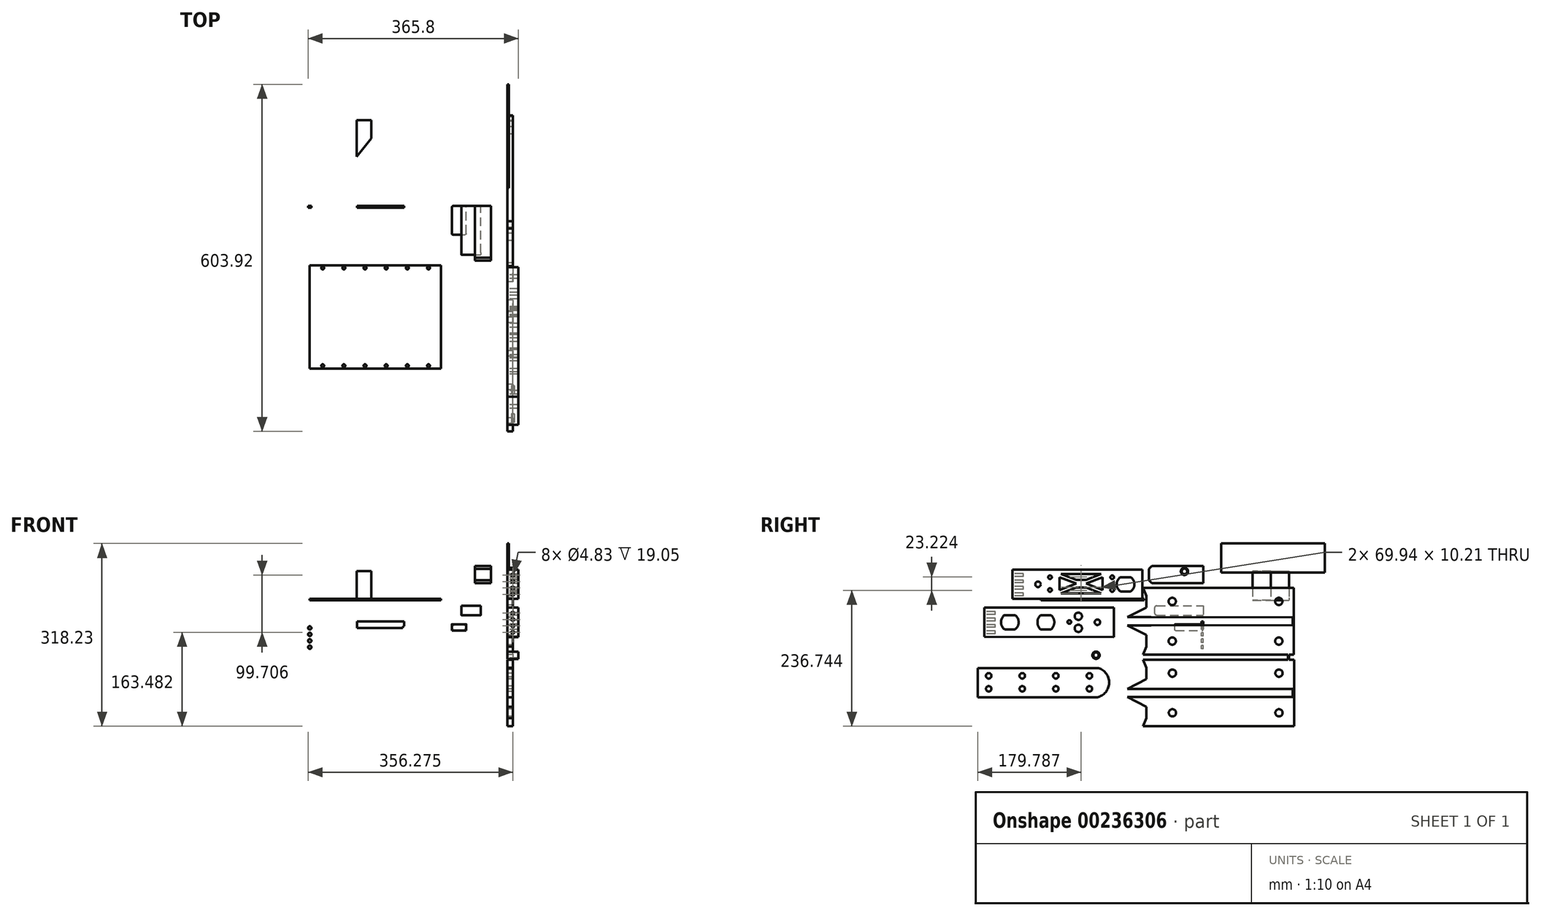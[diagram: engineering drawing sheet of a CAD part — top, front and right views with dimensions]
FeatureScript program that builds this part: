
annotation { "Feature Type Name" : "Feature", "Feature Type Description" : "" }
export const myFeature = defineFeature(function(context is Context, id is Id, definition is map)
    precondition{}
    {
        {
            var Q0;
            Q0=qCreatedBy(makeId("Right.planeOp"),FACE);
            var sketch = newSketch(context, id + "F0", { "sketchPlane" : qUnion([Q0])});
            skPoint(sketch, "E0.1.0.8", {"position": v(-472.48, 27.53) * mm});
            skCircle(sketch, "E1", {"center": v(-287.76, 28) * mm, "radius": 4.76 * mm});
            skLineSegment(sketch, "E2", {"start": v(-233.08, 52.93) * mm, "end": v(-233.08, 40.2) * mm});
            skPoint(sketch, "E2.endSnap0", {"position": v(-233.08, 52.93) * mm});
            skPoint(sketch, "E3.MirrorP", {"position": v(6.32, 27.53) * mm});
            skLineSegment(sketch, "E4", {"start": v(-106.44, 2.48) * mm, "end": v(-332.21, 2.71) * mm});
            skLineSegment(sketch, "E5", {"start": v(-106.44, 53.64) * mm, "end": v(-332.21, 53.6) * mm});
            skCircle(sketch, "E6", {"center": v(-135.36, 28) * mm, "radius": 6.35 * mm});
            skLineSegment(sketch, "E7", {"start": v(-106.44, 53.64) * mm, "end": v(-106.44, 2.48) * mm});
            skPoint(sketch, "E8", {"position": v(-106.44, 28.06) * mm});
            skLineSegment(sketch, "E9", {"start": v(-332.21, 53.6) * mm, "end": v(-332.21, 2.71) * mm});
            skLineSegment(sketch, "E10.bottom", {"start": v(-144.38, 40.44) * mm, "end": v(-126.35, 40.44) * mm});
            skLineSegment(sketch, "E10.top", {"start": v(-144.38, 15.55) * mm, "end": v(-126.35, 15.55) * mm});
            skLineSegment(sketch, "E10.left", {"start": v(-144.38, 40.44) * mm, "end": v(-144.38, 15.55) * mm});
            skLineSegment(sketch, "E10.right", {"start": v(-126.35, 40.44) * mm, "end": v(-126.35, 15.55) * mm});
            skLineSegment(sketch, "E11", {"start": v(-135.36, 15.55) * mm, "end": v(-135.36, 24.56) * mm});
            skArc(sketch, "E12", {"start": v(-126.35, 15.55) * mm, "mid": v(-119.96, 28) * mm, "end": v(-126.35, 40.44) * mm});
            skArc(sketch, "E13.MirrorCS", {"start": v(-144.38, 15.55) * mm, "mid": v(-150.77, 28) * mm, "end": v(-144.38, 40.44) * mm});
            skSolve(sketch);
        }
        {
            var Q0;
            Q0=makeQuery(id+"F0.imprint","IMPRINT",FACE,{"disambiguationData":[TD([[makeQuery(id+"F0.imprint","IMPRINT",EDGE,{"derivedFrom":sQuery(id+"F0.wireOp",EDGE,"48NEkoHX-YDjR-4glP-9xDk-O7jPTVT27snB.bottom")}),-1.0]])]});
            var Q1;
            Q1=makeQuery(id+"F0.imprint","IMPRINT",FACE,{"disambiguationData":[TD([[makeQuery(id+"F0.imprint","IMPRINT",EDGE,{"derivedFrom":sQuery(id+"F0.wireOp",EDGE,"6096469f-17e3-4775-aaf3-049bcc5bdd68.0.1.0")}),1.0]])]});
            var Q2;
            Q2=makeQuery(id+"F0.imprint","IMPRINT",FACE,{"disambiguationData":[TD([[makeQuery(id+"F0.imprint","IMPRINT",EDGE,{"derivedFrom":sQuery(id+"F0.wireOp",EDGE,"6096469f-17e3-4775-aaf3-049bcc5bdd68.0.2.0")}),1.0]])]});
            var Q3;
            Q3=makeQuery(id+"F0.imprint","IMPRINT",FACE,{"disambiguationData":[TD([[makeQuery(id+"F0.imprint","IMPRINT",EDGE,{"derivedFrom":sQuery(id+"F0.wireOp",EDGE,"4wjqRqQA-ueKa-S8QN-2kGj-S2SypDfkeyo9.bottom")}),1.0]])]});
            var Q4;
            Q4=makeQuery(id+"F0.imprint","IMPRINT",FACE,{"disambiguationData":[TD([[makeQuery(id+"F0.imprint","IMPRINT",EDGE,{"derivedFrom":sQuery(id+"F0.wireOp",EDGE,"E0.1.0.1")}),-1.0]])]});
            var Q5;
            Q5=makeQuery(id+"F0.imprint","IMPRINT",FACE,{"disambiguationData":[TD([[makeQuery(id+"F0.imprint","IMPRINT",EDGE,{"derivedFrom":sQuery(id+"F0.wireOp",EDGE,"E1")}),-1.0]])]});
            extrude(context, id + "F1", {"entities" : qUnion([Q0, Q1, Q2, Q3, Q4, Q5]), "depth" : 19.05 * mm});
        }
        {
            var Q0;
            Q0=qCreatedBy(makeId("Right.planeOp"),FACE);
            var sketch = newSketch(context, id + "F2", { "sketchPlane" : qUnion([Q0])});
            skCircle(sketch, "E14", {"center": v(-32.9, 50.41) * mm, "radius": 6.35 * mm});
            skCircle(sketch, "E15", {"center": v(-32.9, 50.41) * mm, "radius": 4.76 * mm});
            skSolve(sketch);
        }
        {
            var Q0;
            Q0 = qSketchRegion(id + "F2", true);
            extrude(context, id + "F3", {"entities" : qUnion([Q0]), "depth" : 9.52 * mm});
        }
        {
            var Q0;
            Q0=qCreatedBy(makeId("Right.planeOp"),FACE);
            var sketch = newSketch(context, id + "F4", { "sketchPlane" : qUnion([Q0])});
            skCircle(sketch, "E16", {"center": v(-54.1, -1.8) * mm, "radius": 6.35 * mm});
            skLineSegment(sketch, "E17", {"start": v(33.95, 20.92) * mm, "end": v(33.95, 8.2) * mm});
            skPoint(sketch, "E17.endSnap0", {"position": v(33.95, 20.92) * mm});
            skLineSegment(sketch, "E18", {"start": v(157.46, -29.52) * mm, "end": v(-90.95, -29.25) * mm});
            skLineSegment(sketch, "E19", {"start": v(157.46, 21.64) * mm, "end": v(-90.94, 21.6) * mm});
            skCircle(sketch, "E20", {"center": v(131.33, -1.8) * mm, "radius": 6.35 * mm});
            skLineSegment(sketch, "E21", {"start": v(157.46, 21.64) * mm, "end": v(157.46, -29.52) * mm});
            skLineSegment(sketch, "E22", {"start": v(-90.94, 21.6) * mm, "end": v(-104.93, 21.6) * mm});
            skLineSegment(sketch, "E23", {"start": v(-104.93, 21.6) * mm, "end": v(-99.24, 7.67) * mm});
            skLineSegment(sketch, "E24", {"start": v(-99.24, -12.44) * mm, "end": v(-132.22, -29.25) * mm});
            skLineSegment(sketch, "E25", {"start": v(-132.22, -29.25) * mm, "end": v(-90.95, -29.25) * mm});
            skLineSegment(sketch, "E26", {"start": v(-99.24, 7.67) * mm, "end": v(-99.24, -12.44) * mm});
            skPoint(sketch, "E27", {"position": v(157.46, -3.94) * mm});
            skLineSegment(sketch, "E28", {"start": v(157.46, -29.52) * mm, "end": v(157.46, -43.14) * mm});
            skLineSegment(sketch, "E29", {"start": v(157.46, -36.33) * mm, "end": v(164.9, -36.33) * mm});
            skLineSegment(sketch, "E30.MirrorCS", {"start": v(33.95, -93.58) * mm, "end": v(33.95, -80.86) * mm});
            skLineSegment(sketch, "E31.MirrorCS", {"start": v(-90.94, -94.26) * mm, "end": v(-104.93, -94.26) * mm});
            skLineSegment(sketch, "E32.MirrorCS", {"start": v(-99.24, -60.22) * mm, "end": v(-132.22, -43.41) * mm});
            skLineSegment(sketch, "E33.MirrorCS", {"start": v(157.46, -94.3) * mm, "end": v(157.46, -43.14) * mm});
            skLineSegment(sketch, "E34.MirrorCS", {"start": v(-104.93, -94.26) * mm, "end": v(-99.24, -80.33) * mm});
            skPoint(sketch, "E35.MirrorP", {"position": v(33.95, -93.58) * mm});
            skPoint(sketch, "E36.MirrorP", {"position": v(157.46, -68.72) * mm});
            skCircle(sketch, "E37.MirrorC", {"center": v(-54.1, -70.86) * mm, "radius": 6.35 * mm});
            skCircle(sketch, "E38.MirrorC", {"center": v(131.33, -70.86) * mm, "radius": 6.35 * mm});
            skLineSegment(sketch, "E39.MirrorCS", {"start": v(157.46, -94.3) * mm, "end": v(-90.94, -94.26) * mm});
            skLineSegment(sketch, "E40.MirrorCS", {"start": v(157.46, -43.14) * mm, "end": v(-90.95, -43.41) * mm});
            skLineSegment(sketch, "E41.MirrorCS", {"start": v(-99.24, -80.33) * mm, "end": v(-99.24, -60.22) * mm});
            skLineSegment(sketch, "E42.MirrorCS", {"start": v(-132.22, -43.41) * mm, "end": v(-90.95, -43.41) * mm});
            skLineSegment(sketch, "E43", {"start": v(155.23, -29.52) * mm, "end": v(155.22, -43.14) * mm});
            skLineSegment(sketch, "E44", {"start": v(155.23, -34.67) * mm, "end": v(157.46, -34.67) * mm});
            skCircle(sketch, "E45", {"center": v(-53.77, -126.66) * mm, "radius": 6.35 * mm});
            skLineSegment(sketch, "E46", {"start": v(34.26, -103.93) * mm, "end": v(34.26, -116.65) * mm});
            skPoint(sketch, "E46.endSnap0", {"position": v(34.26, -103.93) * mm});
            skLineSegment(sketch, "E47", {"start": v(157.78, -154.38) * mm, "end": v(-90.63, -154.1) * mm});
            skLineSegment(sketch, "E48", {"start": v(157.78, -103.22) * mm, "end": v(-90.63, -103.25) * mm});
            skCircle(sketch, "E49", {"center": v(131.65, -126.66) * mm, "radius": 6.35 * mm});
            skLineSegment(sketch, "E50", {"start": v(157.78, -103.22) * mm, "end": v(157.78, -154.38) * mm});
            skLineSegment(sketch, "E51", {"start": v(-90.63, -103.25) * mm, "end": v(-104.6, -103.25) * mm});
            skLineSegment(sketch, "E52", {"start": v(-104.6, -103.25) * mm, "end": v(-98.92, -117.18) * mm});
            skLineSegment(sketch, "E53", {"start": v(-98.92, -137.3) * mm, "end": v(-131.9, -154.1) * mm});
            skLineSegment(sketch, "E54", {"start": v(-131.9, -154.1) * mm, "end": v(-90.63, -154.1) * mm});
            skLineSegment(sketch, "E55", {"start": v(-98.92, -117.18) * mm, "end": v(-98.92, -137.3) * mm});
            skPoint(sketch, "E56", {"position": v(157.78, -128.8) * mm});
            skLineSegment(sketch, "E57", {"start": v(157.78, -154.38) * mm, "end": v(157.78, -168) * mm});
            skLineSegment(sketch, "E58", {"start": v(157.78, -161.19) * mm, "end": v(165.2, -161.19) * mm});
            skLineSegment(sketch, "E59.MirrorCS", {"start": v(34.26, -218.44) * mm, "end": v(34.26, -205.72) * mm});
            skLineSegment(sketch, "E60.MirrorCS", {"start": v(-90.63, -219.12) * mm, "end": v(-104.6, -219.12) * mm});
            skLineSegment(sketch, "E61.MirrorCS", {"start": v(-98.92, -185.08) * mm, "end": v(-131.9, -168.27) * mm});
            skLineSegment(sketch, "E62.MirrorCS", {"start": v(157.78, -219.15) * mm, "end": v(157.78, -168) * mm});
            skLineSegment(sketch, "E63.MirrorCS", {"start": v(-104.6, -219.12) * mm, "end": v(-98.92, -205.19) * mm});
            skPoint(sketch, "E64.MirrorP", {"position": v(34.26, -218.44) * mm});
            skPoint(sketch, "E65.MirrorP", {"position": v(157.78, -193.57) * mm});
            skCircle(sketch, "E66.MirrorC", {"center": v(-53.77, -195.71) * mm, "radius": 6.35 * mm});
            skCircle(sketch, "E67.MirrorC", {"center": v(131.65, -195.71) * mm, "radius": 6.35 * mm});
            skLineSegment(sketch, "E68.MirrorCS", {"start": v(157.78, -219.15) * mm, "end": v(-90.63, -219.12) * mm});
            skLineSegment(sketch, "E69.MirrorCS", {"start": v(157.78, -168) * mm, "end": v(-90.63, -168.27) * mm});
            skLineSegment(sketch, "E70.MirrorCS", {"start": v(-98.92, -205.19) * mm, "end": v(-98.92, -185.08) * mm});
            skLineSegment(sketch, "E71.MirrorCS", {"start": v(-131.9, -168.27) * mm, "end": v(-90.63, -168.27) * mm});
            skLineSegment(sketch, "E72", {"start": v(155.55, -154.37) * mm, "end": v(155.54, -168) * mm});
            skLineSegment(sketch, "E73", {"start": v(155.54, -159.52) * mm, "end": v(157.78, -159.53) * mm});
            skLineSegment(sketch, "E74", {"start": v(148.89, -94.3) * mm, "end": v(148.88, -103.22) * mm});
            skLineSegment(sketch, "E75", {"start": v(147.48, -94.3) * mm, "end": v(147.48, -103.22) * mm});
            skSolve(sketch);
        }
        {
            var Q0;
            Q0 = qSketchRegion(id + "F4", true);
            extrude(context, id + "F5", {"entities" : qUnion([Q0]), "depth" : 9.52 * mm});
        }
        {
            var Q0;
            Q0=qCreatedBy(makeId("Right.planeOp"),FACE);
            var sketch = newSketch(context, id + "F6", { "sketchPlane" : qUnion([Q0])});
            skLineSegment(sketch, "E76", {"start": v(-275.22, -14.07) * mm, "end": v(-275.22, -26.8) * mm});
            skPoint(sketch, "E76.endSnap0", {"position": v(-275.22, -14.07) * mm});
            skLineSegment(sketch, "E77", {"start": v(-155.4, -63.65) * mm, "end": v(-381.17, -63.42) * mm});
            skLineSegment(sketch, "E78", {"start": v(-155.4, -12.5) * mm, "end": v(-381.17, -12.57) * mm});
            skCircle(sketch, "E79", {"center": v(-184.32, -38.07) * mm, "radius": 4.76 * mm});
            skLineSegment(sketch, "E80", {"start": v(-155.4, -12.5) * mm, "end": v(-155.4, -63.65) * mm});
            skPoint(sketch, "E81", {"position": v(-155.4, -38.07) * mm});
            skLineSegment(sketch, "E82", {"start": v(-381.17, -12.57) * mm, "end": v(-381.17, -63.42) * mm});
            skLineSegment(sketch, "E83.bottom", {"start": v(-345.74, -25.63) * mm, "end": v(-327.7, -25.63) * mm});
            skLineSegment(sketch, "E83.top", {"start": v(-345.74, -50.52) * mm, "end": v(-327.7, -50.52) * mm});
            skLineSegment(sketch, "E83.left", {"start": v(-345.74, -25.63) * mm, "end": v(-345.74, -50.52) * mm});
            skLineSegment(sketch, "E83.right", {"start": v(-327.7, -25.63) * mm, "end": v(-327.7, -50.52) * mm});
            skPoint(sketch, "E83.middle", {"position": v(-336.72, -38.08) * mm});
            skLineSegment(sketch, "E84", {"start": v(-336.72, -50.52) * mm, "end": v(-336.72, -39.25) * mm});
            skArc(sketch, "E85", {"start": v(-327.7, -50.52) * mm, "mid": v(-321.32, -38.08) * mm, "end": v(-327.7, -25.63) * mm});
            skArc(sketch, "E86.MirrorCS", {"start": v(-345.74, -50.52) * mm, "mid": v(-352.12, -38.08) * mm, "end": v(-345.74, -25.63) * mm});
            skSolve(sketch);
        }
        {
            var Q0;
            Q0=makeQuery(id+"F6.imprint","IMPRINT",FACE,{"disambiguationData":[TD([[makeQuery(id+"F6.imprint","IMPRINT",EDGE,{"derivedFrom":sQuery(id+"F6.wireOp",EDGE,"E77")}),-1.0]])]});
            extrude(context, id + "F7", {"entities" : qUnion([Q0]), "depth" : 19.05 * mm});
        }
        {
            var Q0;
            Q0=qCreatedBy(makeId("Front.planeOp"),FACE);
            var sketch = newSketch(context, id + "F8", { "sketchPlane" : qUnion([Q0])});
            skLineSegment(sketch, "E87.bottom", {"start": v(-56.23, 29.85) * mm, "end": v(-28.23, 29.85) * mm});
            skLineSegment(sketch, "E87.top", {"start": v(-56.23, 59.85) * mm, "end": v(-28.23, 59.85) * mm});
            skLineSegment(sketch, "E87.left", {"start": v(-56.23, 29.85) * mm, "end": v(-56.23, 59.85) * mm});
            skLineSegment(sketch, "E87.right", {"start": v(-28.23, 29.85) * mm, "end": v(-28.23, 59.85) * mm});
            skSolve(sketch);
        }
        {
            var Q0;
            Q0 = qSketchRegion(id + "F8", true);
            extrude(context, id + "F9", {"entities" : qUnion([Q0]), "depth" : 95 * mm});
        }
        {
            var Q0;
            Q0=makeQuery(id+"F9.opExtrude","CAP_EDGE",EDGE,{"disambiguationData":[OSD([sQuery(id+"F8.wireOp",EDGE,"E87.top")])],"isStart":false});
            var Q1;
            Q1=makeQuery(id+"F9.opExtrude","CAP_EDGE",EDGE,{"disambiguationData":[OSD([sQuery(id+"F8.wireOp",EDGE,"E87.bottom")])],"isStart":false});
            chamfer(context, id + "F10", {"entities" : qUnion([Q0, Q1]), "width" : 5.08 * mm, "tangentPropagation" : true});
        }
        {
            var Q0;
            Q0=qCreatedBy(makeId("Right.planeOp"),FACE);
            var sketch = newSketch(context, id + "F11", { "sketchPlane" : qUnion([Q0])});
            skCircle(sketch, "E88", {"center": v(-186.77, -95.44) * mm, "radius": 4.76 * mm});
            skCircle(sketch, "E89", {"center": v(-186.77, -95.44) * mm, "radius": 6.35 * mm});
            skSolve(sketch);
        }
        {
            var Q0;
            Q0 = qSketchRegion(id + "F11", true);
            extrude(context, id + "F12", {"entities" : qUnion([Q0]), "depth" : 19.05 * mm});
        }
        {
            var Q0;
            Q0=qCreatedBy(makeId("Front.planeOp"),FACE);
            var sketch = newSketch(context, id + "F13", { "sketchPlane" : qUnion([Q0])});
            skLineSegment(sketch, "E90.bottom", {"start": v(-96.57, -36.56) * mm, "end": v(-426.77, -36.56) * mm});
            skLineSegment(sketch, "E90.top", {"start": v(-96.57, -100.06) * mm, "end": v(-426.77, -100.06) * mm});
            skLineSegment(sketch, "E90.left", {"start": v(-96.57, -36.56) * mm, "end": v(-96.57, -100.06) * mm});
            skLineSegment(sketch, "E90.right", {"start": v(-426.77, -36.56) * mm, "end": v(-426.77, -100.06) * mm});
            skPoint(sketch, "E90.middle", {"position": v(-261.67, -68.31) * mm});
            skSolve(sketch);
        }
        {
            var Q0;
            Q0 = qSketchRegion(id + "F13", true);
            extrude(context, id + "F14", {"entities" : qUnion([Q0]), "depth" : 3.17 * mm});
        }
        {
            var Q0;
            Q0=makeQuery(id+"F7.opExtrude","SWEPT_FACE",FACE,{"disambiguationData":[OSD([sQuery(id+"F6.wireOp",EDGE,"E82")])]});
            var sketch = newSketch(context, id + "F15", { "sketchPlane" : qUnion([Q0])});
            skCircle(sketch, "E91", {"center": v(9.53, -22.14) * mm, "radius": 2.41 * mm});
            skPoint(sketch, "E91.centerSnap0", {"position": v(9.53, -12.57) * mm});
            skPoint(sketch, "E92.centerSnap0", {"position": v(9.53, -63.42) * mm});
            skCircle(sketch, "E93.0.1.0", {"center": v(9.53, -33.32) * mm, "radius": 2.41 * mm});
            skCircle(sketch, "E93.0.2.0", {"center": v(9.53, -44.5) * mm, "radius": 2.41 * mm});
            skCircle(sketch, "E93.0.3.0", {"center": v(9.53, -55.67) * mm, "radius": 2.41 * mm});
            skLineSegment(sketch, "E93.direction1", {"start": v(9.53, -22.14) * mm, "end": v(34.93, -22.14) * mm, "construction": true});
            skLineSegment(sketch, "E93.direction2", {"start": v(9.53, -22.14) * mm, "end": v(9.53, -33.32) * mm, "construction": true});
            skSolve(sketch);
        }
        {
            var Q0;
            Q0 = qSketchRegion(id + "F15", true);
            extrude(context, id + "F16", {"entities" : qUnion([Q0]), "operationType" : NewBodyOperationType.REMOVE, "oppositeDirection" : true, "depth" : 19.05 * mm});
        }
        {
            var Q0;
            Q0=makeQuery(id+"F1.opExtrude","SWEPT_FACE",FACE,{"disambiguationData":[OSD([sQuery(id+"F0.wireOp",EDGE,"E9")])]});
            var sketch = newSketch(context, id + "F17", { "sketchPlane" : qUnion([Q0])});
            skCircle(sketch, "E94", {"center": v(9.53, 44.04) * mm, "radius": 2.41 * mm});
            skPoint(sketch, "E94.centerSnap0", {"position": v(9.53, 53.6) * mm});
            skLineSegment(sketch, "E95", {"start": v(9.53, 44.04) * mm, "end": v(9.53, 53.6) * mm});
            skCircle(sketch, "E96.0.1.0", {"center": v(9.53, 32.86) * mm, "radius": 2.41 * mm});
            skCircle(sketch, "E96.0.2.0", {"center": v(9.53, 21.69) * mm, "radius": 2.41 * mm});
            skCircle(sketch, "E96.0.3.0", {"center": v(9.53, 10.51) * mm, "radius": 2.41 * mm});
            skLineSegment(sketch, "E96.direction1", {"start": v(9.53, 44.04) * mm, "end": v(34.93, 44.04) * mm, "construction": true});
            skLineSegment(sketch, "E96.direction2", {"start": v(9.53, 44.04) * mm, "end": v(9.53, 32.86) * mm, "construction": true});
            skSolve(sketch);
        }
        {
            var Q0;
            Q0 = qSketchRegion(id + "F17", true);
            extrude(context, id + "F18", {"entities" : qUnion([Q0]), "operationType" : NewBodyOperationType.REMOVE, "oppositeDirection" : true, "depth" : 19.05 * mm});
        }
        {
            var Q0;
            Q0=makeQuery(id+"F14.opExtrude","CAP_FACE",FACE,{"disambiguationData":[OSD([sQuery(id+"F13.wireOp",EDGE,"E90.bottom"),sQuery(id+"F13.wireOp",EDGE,"E90.top"),sQuery(id+"F13.wireOp",EDGE,"E90.left"),sQuery(id+"F13.wireOp",EDGE,"E90.right")])],"isStart":false});
            var sketch = newSketch(context, id + "F19", { "sketchPlane" : qUnion([Q0])});
            skLineSegment(sketch, "E97", {"start": v(-261.67, -36.56) * mm, "end": v(-261.67, -48) * mm});
            skLineSegment(sketch, "E98", {"start": v(-261.67, -48) * mm, "end": v(-179.52, -48) * mm});
            skLineSegment(sketch, "E99", {"start": v(-179.52, -48) * mm, "end": v(-179.52, -36.56) * mm});
            skCircle(sketch, "E100", {"center": v(-179.52, -48) * mm, "radius": 2.92 * mm});
            skCircle(sketch, "E101.0.1.0", {"center": v(-179.52, -59.17) * mm, "radius": 2.92 * mm});
            skCircle(sketch, "E101.0.2.0", {"center": v(-179.52, -70.34) * mm, "radius": 2.92 * mm});
            skCircle(sketch, "E101.0.3.0", {"center": v(-179.52, -81.52) * mm, "radius": 2.92 * mm});
            skLineSegment(sketch, "E101.direction1", {"start": v(-179.52, -48) * mm, "end": v(-171.82, -48) * mm, "construction": true});
            skLineSegment(sketch, "E101.direction2", {"start": v(-179.52, -48) * mm, "end": v(-179.52, -59.17) * mm, "construction": true});
            skCircle(sketch, "E102.MirrorC", {"center": v(-343.83, -81.52) * mm, "radius": 2.92 * mm});
            skCircle(sketch, "E103.MirrorC", {"center": v(-343.83, -48) * mm, "radius": 2.92 * mm});
            skCircle(sketch, "E104.MirrorC", {"center": v(-343.83, -70.34) * mm, "radius": 2.92 * mm});
            skLineSegment(sketch, "E105.MirrorCS", {"start": v(-343.83, -48) * mm, "end": v(-343.83, -59.17) * mm, "construction": true});
            skCircle(sketch, "E106.MirrorC", {"center": v(-343.83, -59.17) * mm, "radius": 2.92 * mm});
            skSolve(sketch);
        }
        {
            var Q0;
            Q0=makeQuery(id+"F19.imprint","IMPRINT",FACE,{"disambiguationData":[TD([[makeQuery(id+"F19.imprint","IMPRINT",EDGE,{"derivedFrom":sQuery(id+"F19.wireOp",EDGE,"E103.MirrorC")}),-1.0]])]});
            var Q1;
            Q1=makeQuery(id+"F19.imprint","IMPRINT",FACE,{"disambiguationData":[TD([[makeQuery(id+"F19.imprint","IMPRINT",EDGE,{"derivedFrom":sQuery(id+"F19.wireOp",EDGE,"E106.MirrorC")}),-1.0]])]});
            var Q2;
            Q2=makeQuery(id+"F19.imprint","IMPRINT",FACE,{"disambiguationData":[TD([[makeQuery(id+"F19.imprint","IMPRINT",EDGE,{"derivedFrom":sQuery(id+"F19.wireOp",EDGE,"E104.MirrorC")}),-1.0]])]});
            var Q3;
            Q3=makeQuery(id+"F19.imprint","IMPRINT",FACE,{"disambiguationData":[TD([[makeQuery(id+"F19.imprint","IMPRINT",EDGE,{"derivedFrom":sQuery(id+"F19.wireOp",EDGE,"E102.MirrorC")}),-1.0]])]});
            var Q4;
            Q4=makeQuery(id+"F19.imprint","IMPRINT",FACE,{"disambiguationData":[TD([[makeQuery(id+"F19.imprint","IMPRINT",EDGE,{"derivedFrom":sQuery(id+"F19.wireOp",EDGE,"E101.0.2.0")}),1.0]])]});
            var Q5;
            Q5=makeQuery(id+"F19.imprint","IMPRINT",FACE,{"disambiguationData":[TD([[makeQuery(id+"F19.imprint","IMPRINT",EDGE,{"derivedFrom":sQuery(id+"F19.wireOp",EDGE,"E101.0.1.0")}),1.0]])]});
            var Q6;
            {var subQ0=sQuery(id+"F19.wireOp",EDGE,"E99");var subQ1=sQuery(id+"F19.wireOp",EDGE,"E98");var subQ2=makeQuery(id+"F19.imprint","INTERSECT",VERTEX,{"derivedFrom":[subQ1,subQ0]});Q6=makeQuery(id+"F19.imprint","IMPRINT",FACE,{"disambiguationData":[TD([[makeQuery(id+"F19.imprint","IMPRINT",EDGE,{"disambiguationData":[TD([[subQ2,1.0]])],"derivedFrom":subQ1}),-1.0]])]});}
            var Q7;
            Q7=makeQuery(id+"F19.imprint","IMPRINT",FACE,{"disambiguationData":[TD([[makeQuery(id+"F19.imprint","IMPRINT",EDGE,{"derivedFrom":sQuery(id+"F19.wireOp",EDGE,"E101.0.3.0")}),1.0]])]});
            var Q8;
            {var subQ0=sQuery(id+"F19.wireOp",EDGE,"E99");var subQ1=sQuery(id+"F19.wireOp",EDGE,"E98");var subQ2=makeQuery(id+"F19.imprint","INTERSECT",VERTEX,{"derivedFrom":[subQ1,subQ0]});Q8=makeQuery(id+"F19.imprint","IMPRINT",FACE,{"disambiguationData":[TD([[makeQuery(id+"F19.imprint","IMPRINT",EDGE,{"disambiguationData":[TD([[subQ2,1.0]])],"derivedFrom":subQ1}),1.0]])]});}
            var Q9;
            Q9=makeQuery(id+"F14.opExtrude","CAP_FACE",FACE,{"disambiguationData":[OSD([sQuery(id+"F13.wireOp",EDGE,"E90.bottom"),sQuery(id+"F13.wireOp",EDGE,"E90.top"),sQuery(id+"F13.wireOp",EDGE,"E90.left"),sQuery(id+"F13.wireOp",EDGE,"E90.right")])],"isStart":true});
            extrude(context, id + "F20", {"entities" : qUnion([Q0, Q1, Q2, Q3, Q4, Q5, Q6, Q7, Q8]), "operationType" : NewBodyOperationType.REMOVE, "endBound" : BoundingType.UP_TO_SURFACE, "oppositeDirection" : true, "endBoundEntityFace" : qUnion([Q9]), "depth" : 25.4 * mm});
        }
        {
            var Q0;
            Q0=qCreatedBy(makeId("Top.planeOp"),FACE);
            var sketch = newSketch(context, id + "F21", { "sketchPlane" : qUnion([Q0])});
            skLineSegment(sketch, "E107.bottom", {"start": v(-115.3, -103.27) * mm, "end": v(-343.9, -103.27) * mm});
            skLineSegment(sketch, "E107.top", {"start": v(-115.3, -282.94) * mm, "end": v(-343.9, -282.94) * mm});
            skLineSegment(sketch, "E107.left", {"start": v(-115.3, -103.27) * mm, "end": v(-115.3, -282.94) * mm});
            skLineSegment(sketch, "E107.right", {"start": v(-343.9, -103.27) * mm, "end": v(-343.9, -282.94) * mm});
            skSolve(sketch);
        }
        {
            var Q0;
            Q0 = qSketchRegion(id + "F21", true);
            extrude(context, id + "F22", {"entities" : qUnion([Q0]), "depth" : 2.54 * mm});
        }
        {
            var Q0;
            Q0=qCreatedBy(makeId("Front.planeOp"),FACE);
            var sketch = newSketch(context, id + "F23", { "sketchPlane" : qUnion([Q0])});
            skLineSegment(sketch, "E108.bottom", {"start": v(-80, -9.56) * mm, "end": v(-46, -9.56) * mm});
            skLineSegment(sketch, "E108.top", {"start": v(-80, -25.56) * mm, "end": v(-46, -25.56) * mm});
            skLineSegment(sketch, "E108.left", {"start": v(-80, -9.56) * mm, "end": v(-80, -25.56) * mm});
            skLineSegment(sketch, "E108.right", {"start": v(-46, -9.56) * mm, "end": v(-46, -25.56) * mm});
            skSolve(sketch);
        }
        {
            var Q0;
            Q0 = qSketchRegion(id + "F23", true);
            extrude(context, id + "F24", {"entities" : qUnion([Q0]), "depth" : 85 * mm});
        }
        {
            var Q0;
            Q0=makeQuery(id+"F24.opExtrude","CAP_EDGE",EDGE,{"disambiguationData":[OSD([sQuery(id+"F23.wireOp",EDGE,"E108.top")])],"isStart":false});
            var Q1;
            Q1=makeQuery(id+"F24.opExtrude","CAP_EDGE",EDGE,{"disambiguationData":[OSD([sQuery(id+"F23.wireOp",EDGE,"E108.bottom")])],"isStart":false});
            fillet(context, id + "F25", {"entities" : qUnion([Q0, Q1]), "radius" : 3.8 * mm, "tangentPropagation" : true, "allowEdgeOverflow" : false});
        }
        {
            var Q0;
            Q0=qCreatedBy(makeId("Front.planeOp"),FACE);
            var sketch = newSketch(context, id + "F26", { "sketchPlane" : qUnion([Q0])});
            skLineSegment(sketch, "E109.bottom", {"start": v(-96.6, -41.43) * mm, "end": v(-71.6, -41.43) * mm});
            skLineSegment(sketch, "E109.top", {"start": v(-96.6, -52.43) * mm, "end": v(-71.6, -52.43) * mm});
            skLineSegment(sketch, "E109.left", {"start": v(-96.6, -41.43) * mm, "end": v(-96.6, -52.43) * mm});
            skLineSegment(sketch, "E109.right", {"start": v(-71.6, -41.43) * mm, "end": v(-71.6, -52.43) * mm});
            skSolve(sketch);
        }
        {
            var Q0;
            Q0 = qSketchRegion(id + "F26", true);
            extrude(context, id + "F27", {"entities" : qUnion([Q0]), "depth" : 50 * mm});
        }
        {
            var Q0;
            Q0=makeQuery(id+"F27.opExtrude","CAP_EDGE",EDGE,{"disambiguationData":[OSD([sQuery(id+"F26.wireOp",EDGE,"E109.bottom")])],"isStart":false});
            var Q1;
            Q1=makeQuery(id+"F27.opExtrude","CAP_EDGE",EDGE,{"disambiguationData":[OSD([sQuery(id+"F26.wireOp",EDGE,"E109.left")])],"isStart":false});
            var Q2;
            Q2=makeQuery(id+"F27.opExtrude","CAP_EDGE",EDGE,{"disambiguationData":[OSD([sQuery(id+"F26.wireOp",EDGE,"E109.top")])],"isStart":false});
            var Q3;
            Q3=makeQuery(id+"F27.opExtrude","CAP_EDGE",EDGE,{"disambiguationData":[OSD([sQuery(id+"F26.wireOp",EDGE,"E109.right")])],"isStart":false});
            fillet(context, id + "F28", {"entities" : qUnion([Q0, Q1, Q2, Q3]), "radius" : 1.9 * mm, "tangentPropagation" : true, "allowEdgeOverflow" : false});
        }
        {
            var Q0;
            Q0=makeQuery(id+"F27.opExtrude","CAP_EDGE",EDGE,{"disambiguationData":[OSD([sQuery(id+"F26.wireOp",EDGE,"E109.right")])],"isStart":true});
            var Q1;
            Q1=makeQuery(id+"F27.opExtrude","CAP_EDGE",EDGE,{"disambiguationData":[OSD([sQuery(id+"F26.wireOp",EDGE,"E109.bottom")])],"isStart":true});
            var Q2;
            Q2=makeQuery(id+"F27.opExtrude","CAP_EDGE",EDGE,{"disambiguationData":[OSD([sQuery(id+"F26.wireOp",EDGE,"E109.left")])],"isStart":true});
            var Q3;
            Q3=makeQuery(id+"F27.opExtrude","CAP_EDGE",EDGE,{"disambiguationData":[OSD([sQuery(id+"F26.wireOp",EDGE,"E109.top")])],"isStart":true});
            fillet(context, id + "F29", {"entities" : qUnion([Q0, Q1, Q2, Q3]), "radius" : 2.54 * mm, "tangentPropagation" : true, "allowEdgeOverflow" : false});
        }
        {
            var Q0;
            Q0=makeQuery(id+"F7.opExtrude","CAP_FACE",FACE,{"disambiguationData":[OSD([sQuery(id+"F6.wireOp",EDGE,"E77"),sQuery(id+"F6.wireOp",EDGE,"E78"),sQuery(id+"F6.wireOp",EDGE,"E79"),sQuery(id+"F6.wireOp",EDGE,"E80"),sQuery(id+"F6.wireOp",EDGE,"E82"),sQuery(id+"F6.wireOp",EDGE,"E83.bottom"),sQuery(id+"F6.wireOp",EDGE,"E83.top"),sQuery(id+"F6.wireOp",EDGE,"E85"),sQuery(id+"F6.wireOp",EDGE,"E86.MirrorCS")])],"isStart":true});
            var sketch = newSketch(context, id + "F30", { "sketchPlane" : qUnion([Q0])});
            skPoint(sketch, "E110.startSnap0", {"position": v(155.4, -38.07) * mm});
            skLineSegment(sketch, "E111.bottom", {"start": v(283.04, -50.52) * mm, "end": v(264.96, -50.52) * mm});
            skLineSegment(sketch, "E111.top", {"start": v(283.04, -25.63) * mm, "end": v(264.96, -25.63) * mm});
            skLineSegment(sketch, "E111.left", {"start": v(283.04, -50.52) * mm, "end": v(283.04, -25.63) * mm});
            skLineSegment(sketch, "E111.right", {"start": v(264.96, -50.52) * mm, "end": v(264.96, -25.63) * mm});
            skArc(sketch, "E112", {"start": v(264.96, -25.63) * mm, "mid": v(259.33, -38.08) * mm, "end": v(264.96, -50.52) * mm});
            skLineSegment(sketch, "E113", {"start": v(274, -50.52) * mm, "end": v(274, -43.97) * mm});
            skArc(sketch, "E114.MirrorCS", {"start": v(283.04, -25.63) * mm, "mid": v(288.67, -38.08) * mm, "end": v(283.04, -50.52) * mm});
            skCircle(sketch, "E115", {"center": v(217.54, -27.64) * mm, "radius": 6.35 * mm});
            skCircle(sketch, "E116", {"center": v(217.54, -48.64) * mm, "radius": 6.35 * mm});
            skCircle(sketch, "E117", {"center": v(233.2, -37.64) * mm, "radius": 3.18 * mm});
            skSolve(sketch);
        }
        {
            var Q0;
            Q0 = qSketchRegion(id + "F30", true);
            extrude(context, id + "F31", {"entities" : qUnion([Q0]), "operationType" : NewBodyOperationType.REMOVE, "endBound" : BoundingType.THROUGH_ALL, "oppositeDirection" : true, "depth" : 25.4 * mm});
        }
        {
            var Q0;
            Q0=makeQuery(id+"F1.opExtrude","CAP_FACE",FACE,{"disambiguationData":[OSD([sQuery(id+"F0.wireOp",EDGE,"E1"),sQuery(id+"F0.wireOp",EDGE,"E4"),sQuery(id+"F0.wireOp",EDGE,"E5"),sQuery(id+"F0.wireOp",EDGE,"E7"),sQuery(id+"F0.wireOp",EDGE,"E9"),sQuery(id+"F0.wireOp",EDGE,"E10.bottom"),sQuery(id+"F0.wireOp",EDGE,"E10.top"),sQuery(id+"F0.wireOp",EDGE,"E12"),sQuery(id+"F0.wireOp",EDGE,"E13.MirrorCS")])],"isStart":true});
            var sketch = newSketch(context, id + "F32", { "sketchPlane" : qUnion([Q0])});
            skPoint(sketch, "E118.centerSnap0", {"position": v(159.15, 32.56) * mm});
            skLineSegment(sketch, "E119", {"start": v(236.07, 62.12) * mm, "end": v(227.18, 62.12) * mm});
            skLineSegment(sketch, "E120", {"start": v(227.18, 62.12) * mm, "end": v(227.18, 57.76) * mm});
            skLineSegment(sketch, "E121", {"start": v(204.12, 29.2) * mm, "end": v(175.41, 40.32) * mm});
            skLineSegment(sketch, "E122", {"start": v(175.41, 40.32) * mm, "end": v(175.41, 29.2) * mm});
            skLineSegment(sketch, "E123", {"start": v(212.7, 29.2) * mm, "end": v(218.97, 29.2) * mm});
            skLineSegment(sketch, "E124.MirrorCS", {"start": v(204.12, 29.2) * mm, "end": v(175.41, 18.1) * mm});
            skLineSegment(sketch, "E125.MirrorCS", {"start": v(175.41, 18.1) * mm, "end": v(175.41, 29.2) * mm});
            skLineSegment(sketch, "E126.MirrorCS", {"start": v(221.28, 29.2) * mm, "end": v(250, 40.32) * mm});
            skLineSegment(sketch, "E127.MirrorCS", {"start": v(221.28, 29.2) * mm, "end": v(250, 18.1) * mm});
            skLineSegment(sketch, "E128.MirrorCS", {"start": v(250, 40.32) * mm, "end": v(250, 29.2) * mm});
            skLineSegment(sketch, "E129.MirrorCS", {"start": v(250, 18.1) * mm, "end": v(250, 29.2) * mm});
            skLineSegment(sketch, "E130", {"start": v(204.12, 22.7) * mm, "end": v(177.73, 12.49) * mm});
            skLineSegment(sketch, "E131", {"start": v(177.73, 12.49) * mm, "end": v(212.7, 12.49) * mm});
            skLineSegment(sketch, "E132", {"start": v(212.7, 12.49) * mm, "end": v(212.7, 22.7) * mm});
            skLineSegment(sketch, "E133", {"start": v(212.7, 22.7) * mm, "end": v(204.12, 22.7) * mm});
            skLineSegment(sketch, "E134.MirrorCS", {"start": v(212.7, 22.7) * mm, "end": v(221.28, 22.7) * mm});
            skLineSegment(sketch, "E135.MirrorCS", {"start": v(221.28, 22.7) * mm, "end": v(247.67, 12.49) * mm});
            skLineSegment(sketch, "E136.MirrorCS", {"start": v(247.67, 12.49) * mm, "end": v(212.7, 12.49) * mm});
            skLineSegment(sketch, "E137.MirrorCS", {"start": v(221.28, 35.71) * mm, "end": v(247.67, 45.93) * mm});
            skLineSegment(sketch, "E138.MirrorCS", {"start": v(212.7, 35.71) * mm, "end": v(221.28, 35.71) * mm});
            skLineSegment(sketch, "E139.MirrorCS", {"start": v(212.7, 35.71) * mm, "end": v(204.12, 35.71) * mm});
            skLineSegment(sketch, "E140.MirrorCS", {"start": v(212.7, 45.93) * mm, "end": v(212.7, 35.71) * mm});
            skLineSegment(sketch, "E141.MirrorCS", {"start": v(204.12, 35.71) * mm, "end": v(177.73, 45.93) * mm});
            skLineSegment(sketch, "E142.MirrorCS", {"start": v(247.67, 45.93) * mm, "end": v(212.7, 45.93) * mm});
            skLineSegment(sketch, "E143.MirrorCS", {"start": v(177.73, 45.93) * mm, "end": v(212.7, 45.93) * mm});
            skCircle(sketch, "E144", {"center": v(158.58, 40.32) * mm, "radius": 3.18 * mm});
            skCircle(sketch, "E145.MirrorC", {"center": v(266.82, 40.32) * mm, "radius": 3.18 * mm});
            skCircle(sketch, "E146.MirrorC", {"center": v(158.58, 18.1) * mm, "radius": 3.18 * mm});
            skCircle(sketch, "E147.MirrorC", {"center": v(266.82, 18.1) * mm, "radius": 3.18 * mm});
            skSolve(sketch);
        }
        {
            var Q0;
            Q0 = qSketchRegion(id + "F32", true);
            extrude(context, id + "F33", {"entities" : qUnion([Q0]), "operationType" : NewBodyOperationType.REMOVE, "endBound" : BoundingType.THROUGH_ALL, "oppositeDirection" : true, "depth" : 25.4 * mm});
        }
        {
            var Q0;
            Q0=qCreatedBy(makeId("Right.planeOp"),FACE);
            var sketch = newSketch(context, id + "F34", { "sketchPlane" : qUnion([Q0])});
            skLineSegment(sketch, "E148.bottom", {"start": v(31.1, 48.28) * mm, "end": v(211.43, 48.28) * mm});
            skLineSegment(sketch, "E148.top", {"start": v(31.1, 99.08) * mm, "end": v(211.43, 99.08) * mm});
            skLineSegment(sketch, "E148.left", {"start": v(31.1, 48.28) * mm, "end": v(31.1, 99.08) * mm});
            skLineSegment(sketch, "E148.right", {"start": v(211.43, 48.28) * mm, "end": v(211.43, 99.08) * mm});
            skSolve(sketch);
        }
        {
            var Q0;
            Q0 = qSketchRegion(id + "F34", true);
            extrude(context, id + "F35", {"entities" : qUnion([Q0]), "depth" : 2.54 * mm});
        }
        {
            var Q0;
            Q0=qCreatedBy(makeId("Top.planeOp"),FACE);
            var sketch = newSketch(context, id + "F36", { "sketchPlane" : qUnion([Q0])});
            skLineSegment(sketch, "E149.bottom", {"start": v(-236.98, 85.67) * mm, "end": v(-262.38, 85.67) * mm});
            skLineSegment(sketch, "E149.top", {"start": v(-236.98, 149.17) * mm, "end": v(-262.38, 149.17) * mm});
            skLineSegment(sketch, "E149.left", {"start": v(-236.98, 85.67) * mm, "end": v(-236.98, 149.17) * mm});
            skLineSegment(sketch, "E149.right", {"start": v(-262.38, 85.67) * mm, "end": v(-262.38, 149.17) * mm});
            skLineSegment(sketch, "E150", {"start": v(-236.98, 117.42) * mm, "end": v(-262.38, 85.67) * mm});
            skSolve(sketch);
        }
        {
            var Q0;
            {var subQ0=sQuery(id+"F36.wireOp",EDGE,"E149.top");Q0=makeQuery(id+"F36.imprint","IMPRINT",FACE,{"disambiguationData":[TD([[makeQuery(id+"F36.imprint","IMPRINT",EDGE,{"derivedFrom":subQ0}),1.0]])]});}
            extrude(context, id + "F37", {"entities" : qUnion([Q0]), "depth" : 50.8 * mm});
        }
        {
            var Q0;
            Q0=qCreatedBy(makeId("Right.planeOp"),FACE);
            var sketch = newSketch(context, id + "F38", { "sketchPlane" : qUnion([Q0])});
            skLineSegment(sketch, "E151.bottom", {"start": v(-392.5, -117.82) * mm, "end": v(-163.9, -117.82) * mm});
            skLineSegment(sketch, "E151.top", {"start": v(-392.5, -168.62) * mm, "end": v(-163.9, -168.62) * mm});
            skLineSegment(sketch, "E151.left", {"start": v(-392.5, -117.82) * mm, "end": v(-392.5, -168.62) * mm});
            skLineSegment(sketch, "E151.right", {"start": v(-163.9, -117.82) * mm, "end": v(-163.9, -168.62) * mm});
            skArc(sketch, "E152", {"start": v(-184.43, -168.62) * mm, "mid": v(-163.84, -143.94) * mm, "end": v(-182.56, -117.82) * mm});
            skCircle(sketch, "E153", {"center": v(-373.5, -131.33) * mm, "radius": 4.76 * mm});
            skCircle(sketch, "E154.0.1.0", {"center": v(-373.5, -153.93) * mm, "radius": 4.76 * mm});
            skCircle(sketch, "E154.1.0.0", {"center": v(-315.08, -131.33) * mm, "radius": 4.76 * mm});
            skCircle(sketch, "E154.1.1.0", {"center": v(-315.08, -153.93) * mm, "radius": 4.76 * mm});
            skCircle(sketch, "E154.2.0.0", {"center": v(-256.66, -131.33) * mm, "radius": 4.76 * mm});
            skCircle(sketch, "E154.2.1.0", {"center": v(-256.66, -153.93) * mm, "radius": 4.76 * mm});
            skCircle(sketch, "E154.3.0.0", {"center": v(-198.24, -131.33) * mm, "radius": 4.76 * mm});
            skCircle(sketch, "E154.3.1.0", {"center": v(-198.24, -153.93) * mm, "radius": 4.76 * mm});
            skLineSegment(sketch, "E154.direction1", {"start": v(-373.5, -131.33) * mm, "end": v(-315.08, -131.33) * mm, "construction": true});
            skLineSegment(sketch, "E154.direction2", {"start": v(-373.5, -131.33) * mm, "end": v(-373.5, -153.93) * mm, "construction": true});
            skSolve(sketch);
        }
        {
            var Q0;
            {var subQ0=sQuery(id+"F38.wireOp",EDGE,"E152");var subQ1=sQuery(id+"F38.wireOp",EDGE,"E151.right");var subQ2=makeQuery(id+"F38.imprint","INTERSECT",VERTEX,{"disambiguationData":[OD(0.0)],"derivedFrom":[subQ1,subQ0]});Q0=makeQuery(id+"F38.imprint","IMPRINT",FACE,{"disambiguationData":[TD([[makeQuery(id+"F38.imprint","IMPRINT",EDGE,{"disambiguationData":[TD([[subQ2,-1.0]])],"derivedFrom":subQ1}),1.0]])]});}
            var Q1;
            {var subQ8=sQuery(id+"F38.wireOp",EDGE,"E151.left");Q1=makeQuery(id+"F38.imprint","IMPRINT",FACE,{"disambiguationData":[TD([[makeQuery(id+"F38.imprint","IMPRINT",EDGE,{"derivedFrom":subQ8}),1.0]])]});}
            extrude(context, id + "F39", {"entities" : qUnion([Q0, Q1]), "depth" : 9.52 * mm});
        }
        {
            var Q0;
            Q0=makeQuery(id+"F22.opExtrude","CAP_FACE",FACE,{"disambiguationData":[OSD([sQuery(id+"F21.wireOp",EDGE,"E107.bottom"),sQuery(id+"F21.wireOp",EDGE,"E107.top"),sQuery(id+"F21.wireOp",EDGE,"E107.left"),sQuery(id+"F21.wireOp",EDGE,"E107.right")])],"isStart":false});
            var sketch = newSketch(context, id + "F40", { "sketchPlane" : qUnion([Q0])});
            skLineSegment(sketch, "E155", {"start": v(-343.9, -103.27) * mm, "end": v(-343.9, -112.8) * mm});
            skLineSegment(sketch, "E156", {"start": v(-343.9, -112.8) * mm, "end": v(-115.3, -112.8) * mm});
            skLineSegment(sketch, "E157", {"start": v(-343.9, -193.1) * mm, "end": v(-323.78, -193.1) * mm});
            skLineSegment(sketch, "E158.MirrorCS", {"start": v(-343.9, -282.94) * mm, "end": v(-343.9, -273.41) * mm});
            skLineSegment(sketch, "E159.MirrorCS", {"start": v(-343.9, -273.41) * mm, "end": v(-115.3, -273.41) * mm});
            skCircle(sketch, "E160", {"center": v(-321.38, -108.03) * mm, "radius": 2.54 * mm});
            skPoint(sketch, "E160.centerSnap0", {"position": v(-343.9, -108.03) * mm});
            skCircle(sketch, "E161.1.0.0", {"center": v(-284.55, -108.03) * mm, "radius": 2.54 * mm});
            skCircle(sketch, "E161.2.0.0", {"center": v(-247.72, -108.03) * mm, "radius": 2.54 * mm});
            skCircle(sketch, "E161.3.0.0", {"center": v(-210.89, -108.03) * mm, "radius": 2.54 * mm});
            skCircle(sketch, "E161.4.0.0", {"center": v(-174.06, -108.03) * mm, "radius": 2.54 * mm});
            skCircle(sketch, "E161.5.0.0", {"center": v(-137.23, -108.03) * mm, "radius": 2.54 * mm});
            skLineSegment(sketch, "E161.direction1", {"start": v(-321.38, -108.03) * mm, "end": v(-284.55, -108.03) * mm, "construction": true});
            skCircle(sketch, "E162.MirrorC", {"center": v(-284.55, -278.18) * mm, "radius": 2.54 * mm});
            skCircle(sketch, "E163.MirrorC", {"center": v(-321.38, -278.18) * mm, "radius": 2.54 * mm});
            skCircle(sketch, "E164.MirrorC", {"center": v(-247.72, -278.18) * mm, "radius": 2.54 * mm});
            skCircle(sketch, "E165.MirrorC", {"center": v(-174.06, -278.18) * mm, "radius": 2.54 * mm});
            skCircle(sketch, "E166.MirrorC", {"center": v(-137.23, -278.18) * mm, "radius": 2.54 * mm});
            skCircle(sketch, "E167.MirrorC", {"center": v(-210.89, -278.18) * mm, "radius": 2.54 * mm});
            skLineSegment(sketch, "E168.MirrorCS", {"start": v(-321.38, -278.18) * mm, "end": v(-284.55, -278.18) * mm, "construction": true});
            skPoint(sketch, "E169.MirrorP", {"position": v(-343.9, -278.18) * mm});
            skSolve(sketch);
        }
        {
            var Q0;
            Q0 = qSketchRegion(id + "F40", true);
            extrude(context, id + "F41", {"entities" : qUnion([Q0]), "operationType" : NewBodyOperationType.REMOVE, "endBound" : BoundingType.THROUGH_ALL, "oppositeDirection" : true, "depth" : 25.4 * mm});
        }
    });
